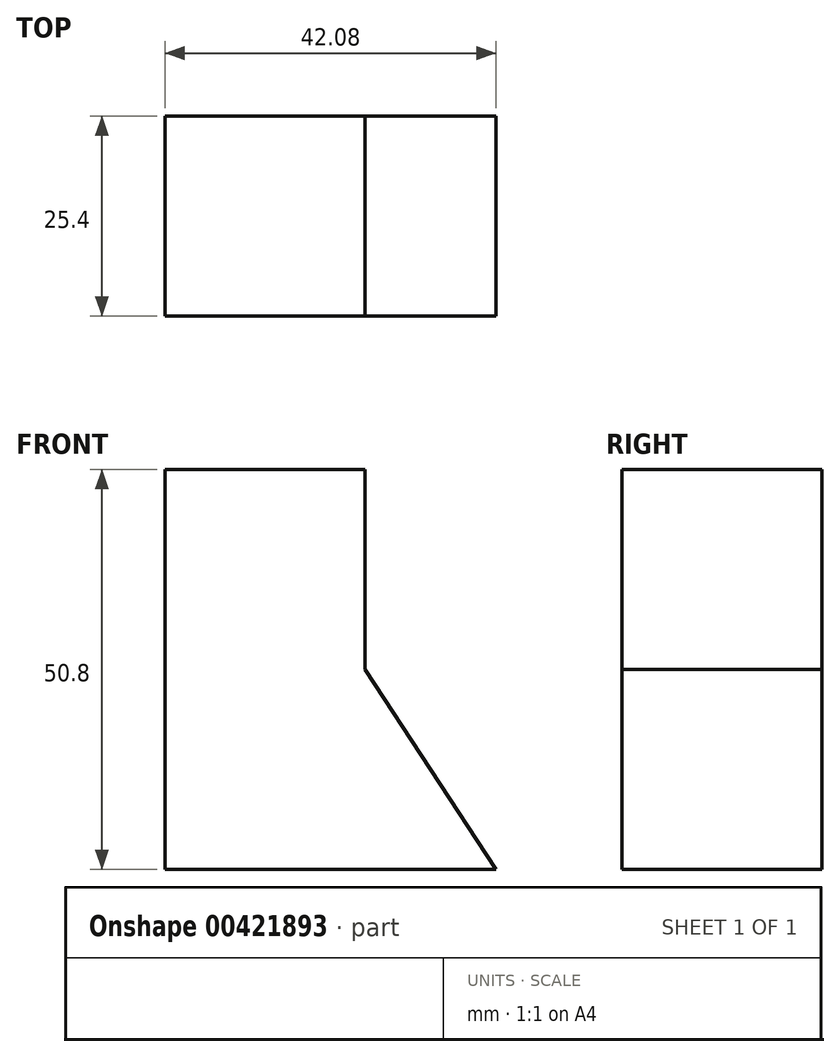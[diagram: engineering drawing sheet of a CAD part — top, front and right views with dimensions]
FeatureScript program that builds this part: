
annotation { "Feature Type Name" : "Feature", "Feature Type Description" : "" }
export const myFeature = defineFeature(function(context is Context, id is Id, definition is map)
    precondition{}
    {
        {
            var Q0;
            Q0=qCreatedBy(makeId("Front.planeOp"),FACE);
            var sketch = newSketch(context, id + "F0", { "sketchPlane" : qUnion([Q0])});
            skLineSegment(sketch, "E0", {"start": v(0, 0) * mm, "end": v(0, 50.8) * mm});
            skLineSegment(sketch, "E1", {"start": v(0, 0) * mm, "end": v(42.08, 0) * mm});
            skLineSegment(sketch, "E2", {"start": v(0, 50.8) * mm, "end": v(25.4, 50.8) * mm});
            skLineSegment(sketch, "E3", {"start": v(25.4, 50.8) * mm, "end": v(25.4, 25.4) * mm});
            skLineSegment(sketch, "E4", {"start": v(25.4, 25.4) * mm, "end": v(42.08, 0) * mm});
            skSolve(sketch);
        }
        {
            var Q0;
            Q0=makeQuery(id+"F0.imprint","IMPRINT",FACE,{"disambiguationData":[TD([[makeQuery(id+"F0.imprint","IMPRINT",EDGE,{"derivedFrom":sQuery(id+"F0.wireOp",EDGE,"E0")}),-1.0]])]});
            extrude(context, id + "F1", {"entities" : qUnion([Q0]), "depth" : 25.4 * mm});
        }
    });
